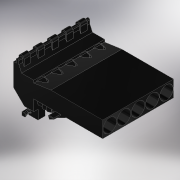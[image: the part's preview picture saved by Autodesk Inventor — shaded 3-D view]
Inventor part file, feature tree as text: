
AUTODESK INVENTOR PART (.ipt)
format: ipt  version: 2018 (Build 220112000, 112)  size: 739,328 bytes
history: native  units: in
note: dims shown in document units (in); Inventor stores cm internally (conversion verified against a paired STEP export)
features: other x15, extrude x15, fillet x3, chamfer x2, pattern_linear x1, sketch x1, projected_geometry x1
ambient origin geometry x8: Origin, YZ Plane, XZ Plane, XY Plane, X Axis, Y Axis, Z Axis, Center Point
bodies: Solid1 (feature_tree)
feature tree (38):
  other  "Base Sketch"
  extrude  "Side Walls"  TaperAngle=0.0deg  [1 undecoded]
  extrude  "Back Wall"  TaperAngle=0.0deg  [1 undecoded]
  extrude  "Front Wall"  TaperAngle=0.0deg  [1 undecoded]
  extrude  "Whistle Housing"  Depth=0.0157in TaperAngle=0.0deg
  extrude  "Tube Socket"  Depth=0.0157in
  other  "Midplane"
  extrude  "Slit"  Depth=0.0157in
  other  "Silicone Fitting"
  extrude  "Silicone Fitting to Chamber"  Depth=0.0157in
  extrude  "Hinge"  Depth=0.0157in
  extrude  "Hinge Nub"  TaperAngle=90.0deg  [1 undecoded]
  chamfer  "Hinge Clearance Chamfer"  Distance=1.5748in
  chamfer  "Spring Pass Chamfer"  Distance=0.3937in
  extrude  "Spring Block"  TaperAngle=0.0deg  [1 undecoded]
  extrude  "Spring Hook"  Depth=0.0157in
  other  "Sping Hook Draft"
  fillet  "Spring Hook Fillet"  Radius=0.4134in
  extrude  "Edge Cut"  TaperAngle=0.0deg  [1 undecoded]
  fillet  "Edge Fillet"  Radius=0.189in
  other  "Pincher Triangle Sketch"
  extrude  "Pincher Triangle"  TaperAngle=0.0deg  [1 undecoded]
  extrude  "Triangle Coupling Male"  Depth=0.0079in
  extrude  "Expand: Triangle Coupling Female"  Depth=0.0787in
  pattern_linear  "Key Repitition"  Spacing1=45.0deg  [1 undecoded]
  fillet  "Fillet: Triangle Coupling Male"  Radius=0.0787in
  sketch  "Sketch5"  dims[d1=0.0in d2=0.0in d3=0.0in d4=0.0in d61=1.5748in d62=0.0in d65=0.0938in d66=0.1181in d67=0.0276in d68=0.0197in d69=90.0deg d71=1.5748in d72=0.0in d78=0.3937in d80=0.0in d81=0.4331in d88=0.4134in d89=0.0in d92=0.189in d93=0.0in d101=0.0079in d105=0.0787in d106=0.1772in d107=45.0deg d112=0.0787in d113=45.0deg d135=0.2067in d136=0.315in d137=0.5906in d139=0.0in d160=0.1181in d161=0.0984in d162=0.3937in d163=0.1575in d164=0.0in d171=1.03in d173=0.4724in d176=0.4134in d177=0.0in d178=0.2067in d179=0.0in d180=0.1374in d181=0.0394in d187=0.2067in d188=0.2362in d190=0.5906in d191=0.0in d193=0.1654in d194=0.0512in d198=0.4134in d199=0.0in d277=0.0079in d278=1.9685in d280=0.4134in d282=0.4134in d283=0.0in d284=0.0394in d285=0.0079in d289=0.0827in d298=0.2067in d299=0.0in d300=0.315in d301=0.0079in d302=0.0394in d303=0.0787in d304=0.0157in]
  projected_geometry  "Projected Loop2"
  other  "Whistle Housing Sketch"
  other  "Edge Cut Sketch"
  other  "Slit Sketch"
  other  "Silicone Fitting Sketch"
  other  "Silicone Fitting to Chamber Sketch"
  other  "Tube Socket Sketch"
  other  "Hinge Sketch"
  other  "Hinge Nub Sketch"
  other  "Spring Block Sketch"
  other  "Spring Hook Sketch"
note: 8 required parameter values undecoded (feature->parameter linkage not recoverable at this tier; creation-order binding heuristic only, values carry confidence <= 0.55)
